annotation { "Feature Type Name" : "Feature", "Feature Type Description" : "" }
export const myFeature = defineFeature(function(context is Context, id is Id, definition is map)
    precondition{}
    {
        {
            var Q0;
            Q0=qCreatedBy(makeId("Top.planeOp"),FACE);
            var sketch = newSketch(context, id + "F0", { "sketchPlane" : qUnion([Q0])});
            skLineSegment(sketch, "E0", {"start": v(-28.2, 6.74) * mm, "end": v(-29.58, 6.6) * mm});
            skLineSegment(sketch, "E1", {"start": v(-29.58, 6.6) * mm, "end": v(-30.85, 6.2) * mm});
            skLineSegment(sketch, "E2", {"start": v(-30.85, 6.2) * mm, "end": v(-32, 5.59) * mm});
            skLineSegment(sketch, "E3", {"start": v(-32, 5.59) * mm, "end": v(-33.01, 4.76) * mm});
            skLineSegment(sketch, "E4", {"start": v(-33.01, 4.76) * mm, "end": v(-33.84, 3.77) * mm});
            skLineSegment(sketch, "E5", {"start": v(-33.84, 3.77) * mm, "end": v(-34.47, 2.62) * mm});
            skLineSegment(sketch, "E6", {"start": v(-34.47, 2.62) * mm, "end": v(-34.86, 1.36) * mm});
            skLineSegment(sketch, "E7", {"start": v(-34.86, 1.36) * mm, "end": v(-35, 0) * mm});
            skLineSegment(sketch, "E8", {"start": v(-35, 0) * mm, "end": v(-34.86, -1.36) * mm});
            skLineSegment(sketch, "E9", {"start": v(-34.86, -1.36) * mm, "end": v(-34.47, -2.62) * mm});
            skLineSegment(sketch, "E10", {"start": v(-34.47, -2.62) * mm, "end": v(-33.84, -3.77) * mm});
            skLineSegment(sketch, "E11", {"start": v(-33.84, -3.77) * mm, "end": v(-33.01, -4.76) * mm});
            skLineSegment(sketch, "E12", {"start": v(-33.01, -4.76) * mm, "end": v(-32, -5.59) * mm});
            skLineSegment(sketch, "E13", {"start": v(-32, -5.59) * mm, "end": v(-30.85, -6.2) * mm});
            skLineSegment(sketch, "E14", {"start": v(-30.85, -6.2) * mm, "end": v(-29.58, -6.6) * mm});
            skLineSegment(sketch, "E15", {"start": v(-29.58, -6.6) * mm, "end": v(-28.2, -6.74) * mm});
            skLineSegment(sketch, "E16", {"start": v(-28.2, -6.74) * mm, "end": v(-26.84, -6.6) * mm});
            skLineSegment(sketch, "E17", {"start": v(-26.84, -6.6) * mm, "end": v(-25.56, -6.2) * mm});
            skLineSegment(sketch, "E18", {"start": v(-25.56, -6.2) * mm, "end": v(-24.41, -5.59) * mm});
            skLineSegment(sketch, "E19", {"start": v(-24.41, -5.59) * mm, "end": v(-23.4, -4.76) * mm});
            skLineSegment(sketch, "E20", {"start": v(-23.4, -4.76) * mm, "end": v(-22.58, -3.77) * mm});
            skLineSegment(sketch, "E21", {"start": v(-22.58, -3.77) * mm, "end": v(-21.95, -2.62) * mm});
            skLineSegment(sketch, "E22", {"start": v(-21.95, -2.62) * mm, "end": v(-21.55, -1.36) * mm});
            skLineSegment(sketch, "E23", {"start": v(-21.55, -1.36) * mm, "end": v(-21.42, 0) * mm});
            skLineSegment(sketch, "E24", {"start": v(-21.42, 0) * mm, "end": v(-21.55, 1.36) * mm});
            skLineSegment(sketch, "E25", {"start": v(-21.55, 1.36) * mm, "end": v(-21.95, 2.62) * mm});
            skLineSegment(sketch, "E26", {"start": v(-21.95, 2.62) * mm, "end": v(-22.58, 3.77) * mm});
            skLineSegment(sketch, "E27", {"start": v(-22.58, 3.77) * mm, "end": v(-23.4, 4.76) * mm});
            skLineSegment(sketch, "E28", {"start": v(-23.4, 4.76) * mm, "end": v(-24.41, 5.59) * mm});
            skLineSegment(sketch, "E29", {"start": v(-24.41, 5.59) * mm, "end": v(-25.56, 6.2) * mm});
            skLineSegment(sketch, "E30", {"start": v(-25.56, 6.2) * mm, "end": v(-26.84, 6.6) * mm});
            skLineSegment(sketch, "E31", {"start": v(-26.84, 6.6) * mm, "end": v(-28.2, 6.74) * mm});
            skLineSegment(sketch, "E32", {"start": v(-28.2, -6.34) * mm, "end": v(-29.5, -6.21) * mm});
            skLineSegment(sketch, "E33", {"start": v(-29.5, -6.21) * mm, "end": v(-30.7, -5.84) * mm});
            skLineSegment(sketch, "E34", {"start": v(-30.7, -5.84) * mm, "end": v(-31.78, -5.26) * mm});
            skLineSegment(sketch, "E35", {"start": v(-31.78, -5.26) * mm, "end": v(-32.73, -4.48) * mm});
            skLineSegment(sketch, "E36", {"start": v(-32.73, -4.48) * mm, "end": v(-33.5, -3.54) * mm});
            skLineSegment(sketch, "E37", {"start": v(-33.5, -3.54) * mm, "end": v(-34.1, -2.47) * mm});
            skLineSegment(sketch, "E38", {"start": v(-34.1, -2.47) * mm, "end": v(-34.47, -1.28) * mm});
            skLineSegment(sketch, "E39", {"start": v(-34.47, -1.28) * mm, "end": v(-34.6, 0) * mm});
            skLineSegment(sketch, "E40", {"start": v(-34.6, 0) * mm, "end": v(-34.47, 1.28) * mm});
            skLineSegment(sketch, "E41", {"start": v(-34.47, 1.28) * mm, "end": v(-34.1, 2.47) * mm});
            skLineSegment(sketch, "E42", {"start": v(-34.1, 2.47) * mm, "end": v(-33.5, 3.54) * mm});
            skLineSegment(sketch, "E43", {"start": v(-33.5, 3.54) * mm, "end": v(-32.73, 4.48) * mm});
            skLineSegment(sketch, "E44", {"start": v(-32.73, 4.48) * mm, "end": v(-31.78, 5.25) * mm});
            skLineSegment(sketch, "E45", {"start": v(-31.78, 5.25) * mm, "end": v(-30.7, 5.84) * mm});
            skLineSegment(sketch, "E46", {"start": v(-30.7, 5.84) * mm, "end": v(-29.5, 6.2) * mm});
            skLineSegment(sketch, "E47", {"start": v(-29.5, 6.2) * mm, "end": v(-28.2, 6.34) * mm});
            skLineSegment(sketch, "E48", {"start": v(-28.2, 6.34) * mm, "end": v(-26.92, 6.2) * mm});
            skLineSegment(sketch, "E49", {"start": v(-26.92, 6.2) * mm, "end": v(-25.72, 5.84) * mm});
            skLineSegment(sketch, "E50", {"start": v(-25.72, 5.84) * mm, "end": v(-24.64, 5.25) * mm});
            skLineSegment(sketch, "E51", {"start": v(-24.64, 5.25) * mm, "end": v(-23.69, 4.48) * mm});
            skLineSegment(sketch, "E52", {"start": v(-23.69, 4.48) * mm, "end": v(-22.9, 3.54) * mm});
            skLineSegment(sketch, "E53", {"start": v(-22.9, 3.54) * mm, "end": v(-22.32, 2.47) * mm});
            skLineSegment(sketch, "E54", {"start": v(-22.32, 2.47) * mm, "end": v(-21.95, 1.28) * mm});
            skLineSegment(sketch, "E55", {"start": v(-21.95, 1.28) * mm, "end": v(-21.82, 0) * mm});
            skLineSegment(sketch, "E56", {"start": v(-21.82, 0) * mm, "end": v(-21.95, -1.28) * mm});
            skLineSegment(sketch, "E57", {"start": v(-21.95, -1.28) * mm, "end": v(-22.32, -2.47) * mm});
            skLineSegment(sketch, "E58", {"start": v(-22.32, -2.47) * mm, "end": v(-22.9, -3.54) * mm});
            skLineSegment(sketch, "E59", {"start": v(-22.9, -3.54) * mm, "end": v(-23.69, -4.48) * mm});
            skLineSegment(sketch, "E60", {"start": v(-23.69, -4.48) * mm, "end": v(-24.64, -5.26) * mm});
            skLineSegment(sketch, "E61", {"start": v(-24.64, -5.26) * mm, "end": v(-25.72, -5.84) * mm});
            skLineSegment(sketch, "E62", {"start": v(-25.72, -5.84) * mm, "end": v(-26.92, -6.21) * mm});
            skLineSegment(sketch, "E63", {"start": v(-26.92, -6.21) * mm, "end": v(-28.2, -6.34) * mm});
            skLineSegment(sketch, "E64", {"start": v(-28.76, -0.16) * mm, "end": v(-28.83, -0.32) * mm});
            skLineSegment(sketch, "E65", {"start": v(-28.83, -0.32) * mm, "end": v(-28.9, -0.48) * mm});
            skLineSegment(sketch, "E66", {"start": v(-28.9, -0.48) * mm, "end": v(-30.52, 0.36) * mm});
            skLineSegment(sketch, "E67", {"start": v(-30.52, 0.36) * mm, "end": v(-32.13, 1.2) * mm});
            skLineSegment(sketch, "E68", {"start": v(-32.13, 1.2) * mm, "end": v(-30.96, -0.3) * mm});
            skLineSegment(sketch, "E69", {"start": v(-30.96, -0.3) * mm, "end": v(-29.8, -1.79) * mm});
            skLineSegment(sketch, "E70", {"start": v(-29.8, -1.79) * mm, "end": v(-30.4, -1.85) * mm});
            skLineSegment(sketch, "E71", {"start": v(-30.4, -1.85) * mm, "end": v(-30.98, -1.92) * mm});
            skLineSegment(sketch, "E72", {"start": v(-30.98, -1.92) * mm, "end": v(-30.66, -2.5) * mm});
            skLineSegment(sketch, "E73", {"start": v(-30.66, -2.5) * mm, "end": v(-30.32, -3.1) * mm});
            skLineSegment(sketch, "E74", {"start": v(-30.32, -3.1) * mm, "end": v(-32, -3.65) * mm});
            skLineSegment(sketch, "E75", {"start": v(-32, -3.65) * mm, "end": v(-32.6, -3.84) * mm});
            skLineSegment(sketch, "E76", {"start": v(-32.6, -3.84) * mm, "end": v(-32.92, -3.45) * mm});
            skLineSegment(sketch, "E77", {"start": v(-32.92, -3.45) * mm, "end": v(-33.2, -3.02) * mm});
            skLineSegment(sketch, "E78", {"start": v(-33.2, -3.02) * mm, "end": v(-33.46, -2.57) * mm});
            skLineSegment(sketch, "E79", {"start": v(-33.46, -2.57) * mm, "end": v(-33.67, -2.1) * mm});
            skLineSegment(sketch, "E80", {"start": v(-33.67, -2.1) * mm, "end": v(-33.84, -1.6) * mm});
            skLineSegment(sketch, "E81", {"start": v(-33.84, -1.6) * mm, "end": v(-33.96, -1.08) * mm});
            skLineSegment(sketch, "E82", {"start": v(-33.96, -1.08) * mm, "end": v(-34.04, -0.55) * mm});
            skLineSegment(sketch, "E83", {"start": v(-34.04, -0.55) * mm, "end": v(-34.06, 0) * mm});
            skLineSegment(sketch, "E84", {"start": v(-34.06, 0) * mm, "end": v(-34.02, 0.7) * mm});
            skLineSegment(sketch, "E85", {"start": v(-34.02, 0.7) * mm, "end": v(-33.9, 1.39) * mm});
            skLineSegment(sketch, "E86", {"start": v(-33.9, 1.39) * mm, "end": v(-33.69, 2.04) * mm});
            skLineSegment(sketch, "E87", {"start": v(-33.69, 2.04) * mm, "end": v(-33.41, 2.66) * mm});
            skLineSegment(sketch, "E88", {"start": v(-33.41, 2.66) * mm, "end": v(-33.07, 3.24) * mm});
            skLineSegment(sketch, "E89", {"start": v(-33.07, 3.24) * mm, "end": v(-32.66, 3.77) * mm});
            skLineSegment(sketch, "E90", {"start": v(-32.66, 3.77) * mm, "end": v(-32.2, 4.25) * mm});
            skLineSegment(sketch, "E91", {"start": v(-32.2, 4.25) * mm, "end": v(-31.68, 4.67) * mm});
            skLineSegment(sketch, "E92", {"start": v(-31.68, 4.67) * mm, "end": v(-30.23, 2.25) * mm});
            skLineSegment(sketch, "E93", {"start": v(-30.23, 2.25) * mm, "end": v(-28.76, -0.16) * mm});
            skLineSegment(sketch, "E94", {"start": v(-22.36, 0) * mm, "end": v(-22.47, -1.17) * mm});
            skLineSegment(sketch, "E95", {"start": v(-22.47, -1.17) * mm, "end": v(-22.82, -2.26) * mm});
            skLineSegment(sketch, "E96", {"start": v(-22.82, -2.26) * mm, "end": v(-23.36, -3.25) * mm});
            skLineSegment(sketch, "E97", {"start": v(-23.36, -3.25) * mm, "end": v(-24.07, -4.1) * mm});
            skLineSegment(sketch, "E98", {"start": v(-24.07, -4.1) * mm, "end": v(-24.94, -4.81) * mm});
            skLineSegment(sketch, "E99", {"start": v(-24.94, -4.81) * mm, "end": v(-25.93, -5.35) * mm});
            skLineSegment(sketch, "E100", {"start": v(-25.93, -5.35) * mm, "end": v(-27.03, -5.69) * mm});
            skLineSegment(sketch, "E101", {"start": v(-27.03, -5.69) * mm, "end": v(-28.21, -5.8) * mm});
            skLineSegment(sketch, "E102", {"start": v(-28.21, -5.8) * mm, "end": v(-28.75, -5.78) * mm});
            skLineSegment(sketch, "E103", {"start": v(-28.75, -5.78) * mm, "end": v(-29.28, -5.71) * mm});
            skLineSegment(sketch, "E104", {"start": v(-29.28, -5.71) * mm, "end": v(-29.79, -5.6) * mm});
            skLineSegment(sketch, "E105", {"start": v(-29.79, -5.6) * mm, "end": v(-30.28, -5.43) * mm});
            skLineSegment(sketch, "E106", {"start": v(-30.28, -5.43) * mm, "end": v(-30.75, -5.23) * mm});
            skLineSegment(sketch, "E107", {"start": v(-30.75, -5.23) * mm, "end": v(-31.2, -4.99) * mm});
            skLineSegment(sketch, "E108", {"start": v(-31.2, -4.99) * mm, "end": v(-31.63, -4.71) * mm});
            skLineSegment(sketch, "E109", {"start": v(-31.63, -4.71) * mm, "end": v(-32.03, -4.4) * mm});
            skLineSegment(sketch, "E110", {"start": v(-32.03, -4.4) * mm, "end": v(-31.85, -4.42) * mm});
            skLineSegment(sketch, "E111", {"start": v(-31.85, -4.42) * mm, "end": v(-30.03, -4.64) * mm});
            skLineSegment(sketch, "E112", {"start": v(-30.03, -4.64) * mm, "end": v(-23.6, -1.32) * mm});
            skLineSegment(sketch, "E113", {"start": v(-23.6, -1.32) * mm, "end": v(-22.53, 0.74) * mm});
            skLineSegment(sketch, "E114", {"start": v(-22.53, 0.74) * mm, "end": v(-22.43, 0.93) * mm});
            skLineSegment(sketch, "E115", {"start": v(-22.43, 0.93) * mm, "end": v(-22.36, 0) * mm});
            skLineSegment(sketch, "E116", {"start": v(-22.58, 1.6) * mm, "end": v(-23.88, 0.4) * mm});
            skLineSegment(sketch, "E117", {"start": v(-23.88, 0.4) * mm, "end": v(-24.35, 0) * mm});
            skLineSegment(sketch, "E118", {"start": v(-24.35, 0) * mm, "end": v(-24.64, -0.26) * mm});
            skLineSegment(sketch, "E119", {"start": v(-24.64, -0.26) * mm, "end": v(-24.95, 0.87) * mm});
            skLineSegment(sketch, "E120", {"start": v(-24.95, 0.87) * mm, "end": v(-25.64, 0.4) * mm});
            skLineSegment(sketch, "E121", {"start": v(-25.64, 0.4) * mm, "end": v(-26.1, 0.1) * mm});
            skLineSegment(sketch, "E122", {"start": v(-26.1, 0.1) * mm, "end": v(-27.26, 3.8) * mm});
            skLineSegment(sketch, "E123", {"start": v(-27.26, 3.8) * mm, "end": v(-27.59, 0.22) * mm});
            skLineSegment(sketch, "E124", {"start": v(-27.59, 0.22) * mm, "end": v(-27.98, 0.4) * mm});
            skLineSegment(sketch, "E125", {"start": v(-27.98, 0.4) * mm, "end": v(-29.46, 2.6) * mm});
            skLineSegment(sketch, "E126", {"start": v(-29.46, 2.6) * mm, "end": v(-30.97, 5.12) * mm});
            skLineSegment(sketch, "E127", {"start": v(-30.97, 5.12) * mm, "end": v(-30.66, 5.27) * mm});
            skLineSegment(sketch, "E128", {"start": v(-30.66, 5.27) * mm, "end": v(-30.34, 5.41) * mm});
            skLineSegment(sketch, "E129", {"start": v(-30.34, 5.41) * mm, "end": v(-30, 5.53) * mm});
            skLineSegment(sketch, "E130", {"start": v(-30, 5.53) * mm, "end": v(-29.66, 5.63) * mm});
            skLineSegment(sketch, "E131", {"start": v(-29.66, 5.63) * mm, "end": v(-29.3, 5.7) * mm});
            skLineSegment(sketch, "E132", {"start": v(-29.3, 5.7) * mm, "end": v(-28.95, 5.76) * mm});
            skLineSegment(sketch, "E133", {"start": v(-28.95, 5.76) * mm, "end": v(-28.58, 5.8) * mm});
            skLineSegment(sketch, "E134", {"start": v(-28.58, 5.8) * mm, "end": v(-28.21, 5.8) * mm});
            skLineSegment(sketch, "E135", {"start": v(-28.21, 5.8) * mm, "end": v(-27.23, 5.72) * mm});
            skLineSegment(sketch, "E136", {"start": v(-27.23, 5.72) * mm, "end": v(-26.3, 5.49) * mm});
            skLineSegment(sketch, "E137", {"start": v(-26.3, 5.49) * mm, "end": v(-25.44, 5.11) * mm});
            skLineSegment(sketch, "E138", {"start": v(-25.44, 5.11) * mm, "end": v(-24.65, 4.6) * mm});
            skLineSegment(sketch, "E139", {"start": v(-24.65, 4.6) * mm, "end": v(-23.96, 4) * mm});
            skLineSegment(sketch, "E140", {"start": v(-23.96, 4) * mm, "end": v(-23.38, 3.28) * mm});
            skLineSegment(sketch, "E141", {"start": v(-23.38, 3.28) * mm, "end": v(-22.91, 2.47) * mm});
            skLineSegment(sketch, "E142", {"start": v(-22.91, 2.47) * mm, "end": v(-22.58, 1.6) * mm});
            skLineSegment(sketch, "E143", {"start": v(-18.1, 2.47) * mm, "end": v(-15.89, 2.47) * mm});
            skLineSegment(sketch, "E144", {"start": v(-15.89, 2.47) * mm, "end": v(-15.89, 1.41) * mm});
            skLineSegment(sketch, "E145", {"start": v(-15.89, 1.41) * mm, "end": v(-18, 1.41) * mm});
            skLineSegment(sketch, "E146", {"start": v(-18, 1.41) * mm, "end": v(-18.15, 1.4) * mm});
            skLineSegment(sketch, "E147", {"start": v(-18.15, 1.4) * mm, "end": v(-18.27, 1.38) * mm});
            skLineSegment(sketch, "E148", {"start": v(-18.27, 1.38) * mm, "end": v(-18.37, 1.33) * mm});
            skLineSegment(sketch, "E149", {"start": v(-18.37, 1.33) * mm, "end": v(-18.46, 1.26) * mm});
            skLineSegment(sketch, "E150", {"start": v(-18.46, 1.26) * mm, "end": v(-18.52, 1.17) * mm});
            skLineSegment(sketch, "E151", {"start": v(-18.52, 1.17) * mm, "end": v(-18.57, 1.07) * mm});
            skLineSegment(sketch, "E152", {"start": v(-18.57, 1.07) * mm, "end": v(-18.6, 0.95) * mm});
            skLineSegment(sketch, "E153", {"start": v(-18.6, 0.95) * mm, "end": v(-18.6, 0.8) * mm});
            skLineSegment(sketch, "E154", {"start": v(-18.6, 0.8) * mm, "end": v(-18.6, -0.9) * mm});
            skLineSegment(sketch, "E155", {"start": v(-18.6, -0.9) * mm, "end": v(-18.6, -1.05) * mm});
            skLineSegment(sketch, "E156", {"start": v(-18.6, -1.05) * mm, "end": v(-18.57, -1.17) * mm});
            skLineSegment(sketch, "E157", {"start": v(-18.57, -1.17) * mm, "end": v(-18.52, -1.27) * mm});
            skLineSegment(sketch, "E158", {"start": v(-18.52, -1.27) * mm, "end": v(-18.46, -1.36) * mm});
            skLineSegment(sketch, "E159", {"start": v(-18.46, -1.36) * mm, "end": v(-18.37, -1.42) * mm});
            skLineSegment(sketch, "E160", {"start": v(-18.37, -1.42) * mm, "end": v(-18.27, -1.47) * mm});
            skLineSegment(sketch, "E161", {"start": v(-18.27, -1.47) * mm, "end": v(-18.15, -1.5) * mm});
            skLineSegment(sketch, "E162", {"start": v(-18.15, -1.5) * mm, "end": v(-18, -1.5) * mm});
            skLineSegment(sketch, "E163", {"start": v(-18, -1.5) * mm, "end": v(-15.89, -1.5) * mm});
            skLineSegment(sketch, "E164", {"start": v(-15.89, -1.5) * mm, "end": v(-15.89, -2.57) * mm});
            skLineSegment(sketch, "E165", {"start": v(-15.89, -2.57) * mm, "end": v(-18.1, -2.57) * mm});
            skLineSegment(sketch, "E166", {"start": v(-18.1, -2.57) * mm, "end": v(-18.29, -2.56) * mm});
            skLineSegment(sketch, "E167", {"start": v(-18.29, -2.56) * mm, "end": v(-18.46, -2.54) * mm});
            skLineSegment(sketch, "E168", {"start": v(-18.46, -2.54) * mm, "end": v(-18.62, -2.5) * mm});
            skLineSegment(sketch, "E169", {"start": v(-18.62, -2.5) * mm, "end": v(-18.77, -2.46) * mm});
            skLineSegment(sketch, "E170", {"start": v(-18.77, -2.46) * mm, "end": v(-18.9, -2.4) * mm});
            skLineSegment(sketch, "E171", {"start": v(-18.9, -2.4) * mm, "end": v(-19.04, -2.33) * mm});
            skLineSegment(sketch, "E172", {"start": v(-19.04, -2.33) * mm, "end": v(-19.15, -2.25) * mm});
            skLineSegment(sketch, "E173", {"start": v(-19.15, -2.25) * mm, "end": v(-19.26, -2.15) * mm});
            skLineSegment(sketch, "E174", {"start": v(-19.26, -2.15) * mm, "end": v(-19.36, -2.04) * mm});
            skLineSegment(sketch, "E175", {"start": v(-19.36, -2.04) * mm, "end": v(-19.45, -1.92) * mm});
            skLineSegment(sketch, "E176", {"start": v(-19.45, -1.92) * mm, "end": v(-19.52, -1.79) * mm});
            skLineSegment(sketch, "E177", {"start": v(-19.52, -1.79) * mm, "end": v(-19.58, -1.65) * mm});
            skLineSegment(sketch, "E178", {"start": v(-19.58, -1.65) * mm, "end": v(-19.62, -1.5) * mm});
            skLineSegment(sketch, "E179", {"start": v(-19.62, -1.5) * mm, "end": v(-19.66, -1.34) * mm});
            skLineSegment(sketch, "E180", {"start": v(-19.66, -1.34) * mm, "end": v(-19.68, -1.17) * mm});
            skLineSegment(sketch, "E181", {"start": v(-19.68, -1.17) * mm, "end": v(-19.68, -0.99) * mm});
            skLineSegment(sketch, "E182", {"start": v(-19.68, -0.99) * mm, "end": v(-19.68, 0.9) * mm});
            skLineSegment(sketch, "E183", {"start": v(-19.68, 0.9) * mm, "end": v(-19.68, 1.07) * mm});
            skLineSegment(sketch, "E184", {"start": v(-19.68, 1.07) * mm, "end": v(-19.66, 1.24) * mm});
            skLineSegment(sketch, "E185", {"start": v(-19.66, 1.24) * mm, "end": v(-19.62, 1.4) * mm});
            skLineSegment(sketch, "E186", {"start": v(-19.62, 1.4) * mm, "end": v(-19.58, 1.55) * mm});
            skLineSegment(sketch, "E187", {"start": v(-19.58, 1.55) * mm, "end": v(-19.52, 1.7) * mm});
            skLineSegment(sketch, "E188", {"start": v(-19.52, 1.7) * mm, "end": v(-19.45, 1.82) * mm});
            skLineSegment(sketch, "E189", {"start": v(-19.45, 1.82) * mm, "end": v(-19.36, 1.94) * mm});
            skLineSegment(sketch, "E190", {"start": v(-19.36, 1.94) * mm, "end": v(-19.26, 2.05) * mm});
            skLineSegment(sketch, "E191", {"start": v(-19.26, 2.05) * mm, "end": v(-19.15, 2.15) * mm});
            skLineSegment(sketch, "E192", {"start": v(-19.15, 2.15) * mm, "end": v(-19.04, 2.23) * mm});
            skLineSegment(sketch, "E193", {"start": v(-19.04, 2.23) * mm, "end": v(-18.9, 2.3) * mm});
            skLineSegment(sketch, "E194", {"start": v(-18.9, 2.3) * mm, "end": v(-18.77, 2.36) * mm});
            skLineSegment(sketch, "E195", {"start": v(-18.77, 2.36) * mm, "end": v(-18.62, 2.4) * mm});
            skLineSegment(sketch, "E196", {"start": v(-18.62, 2.4) * mm, "end": v(-18.46, 2.44) * mm});
            skLineSegment(sketch, "E197", {"start": v(-18.46, 2.44) * mm, "end": v(-18.29, 2.46) * mm});
            skLineSegment(sketch, "E198", {"start": v(-18.29, 2.46) * mm, "end": v(-18.1, 2.47) * mm});
            skLineSegment(sketch, "E199", {"start": v(-15.34, 2.47) * mm, "end": v(-12.56, 2.47) * mm});
            skLineSegment(sketch, "E200", {"start": v(-12.56, 2.47) * mm, "end": v(-12.2, 2.45) * mm});
            skLineSegment(sketch, "E201", {"start": v(-12.2, 2.45) * mm, "end": v(-11.88, 2.4) * mm});
            skLineSegment(sketch, "E202", {"start": v(-11.88, 2.4) * mm, "end": v(-11.74, 2.36) * mm});
            skLineSegment(sketch, "E203", {"start": v(-11.74, 2.36) * mm, "end": v(-11.61, 2.31) * mm});
            skLineSegment(sketch, "E204", {"start": v(-11.61, 2.31) * mm, "end": v(-11.5, 2.26) * mm});
            skLineSegment(sketch, "E205", {"start": v(-11.5, 2.26) * mm, "end": v(-11.4, 2.2) * mm});
            skLineSegment(sketch, "E206", {"start": v(-11.4, 2.2) * mm, "end": v(-11.31, 2.12) * mm});
            skLineSegment(sketch, "E207", {"start": v(-11.31, 2.12) * mm, "end": v(-11.23, 2.04) * mm});
            skLineSegment(sketch, "E208", {"start": v(-11.23, 2.04) * mm, "end": v(-11.17, 1.95) * mm});
            skLineSegment(sketch, "E209", {"start": v(-11.17, 1.95) * mm, "end": v(-11.12, 1.85) * mm});
            skLineSegment(sketch, "E210", {"start": v(-11.12, 1.85) * mm, "end": v(-11.08, 1.74) * mm});
            skLineSegment(sketch, "E211", {"start": v(-11.08, 1.74) * mm, "end": v(-11.05, 1.62) * mm});
            skLineSegment(sketch, "E212", {"start": v(-11.05, 1.62) * mm, "end": v(-11.03, 1.5) * mm});
            skLineSegment(sketch, "E213", {"start": v(-11.03, 1.5) * mm, "end": v(-11.02, 1.36) * mm});
            skLineSegment(sketch, "E214", {"start": v(-11.02, 1.36) * mm, "end": v(-11.02, 0.96) * mm});
            skLineSegment(sketch, "E215", {"start": v(-11.02, 0.96) * mm, "end": v(-11.03, 0.75) * mm});
            skLineSegment(sketch, "E216", {"start": v(-11.03, 0.75) * mm, "end": v(-11.06, 0.56) * mm});
            skLineSegment(sketch, "E217", {"start": v(-11.06, 0.56) * mm, "end": v(-11.11, 0.4) * mm});
            skLineSegment(sketch, "E218", {"start": v(-11.11, 0.4) * mm, "end": v(-11.19, 0.26) * mm});
            skLineSegment(sketch, "E219", {"start": v(-11.19, 0.26) * mm, "end": v(-11.28, 0.14) * mm});
            skLineSegment(sketch, "E220", {"start": v(-11.28, 0.14) * mm, "end": v(-11.4, 0.04) * mm});
            skLineSegment(sketch, "E221", {"start": v(-11.4, 0.04) * mm, "end": v(-11.53, -0.04) * mm});
            skLineSegment(sketch, "E222", {"start": v(-11.53, -0.04) * mm, "end": v(-11.68, -0.1) * mm});
            skLineSegment(sketch, "E223", {"start": v(-11.68, -0.1) * mm, "end": v(-11.58, -0.15) * mm});
            skLineSegment(sketch, "E224", {"start": v(-11.58, -0.15) * mm, "end": v(-11.5, -0.21) * mm});
            skLineSegment(sketch, "E225", {"start": v(-11.5, -0.21) * mm, "end": v(-11.41, -0.29) * mm});
            skLineSegment(sketch, "E226", {"start": v(-11.41, -0.29) * mm, "end": v(-11.34, -0.38) * mm});
            skLineSegment(sketch, "E227", {"start": v(-11.34, -0.38) * mm, "end": v(-11.14, -0.87) * mm});
            skLineSegment(sketch, "E228", {"start": v(-11.14, -0.87) * mm, "end": v(-10.78, -2.57) * mm});
            skLineSegment(sketch, "E229", {"start": v(-10.78, -2.57) * mm, "end": v(-11.9, -2.57) * mm});
            skLineSegment(sketch, "E230", {"start": v(-11.9, -2.57) * mm, "end": v(-12.16, -1.2) * mm});
            skLineSegment(sketch, "E231", {"start": v(-12.16, -1.2) * mm, "end": v(-12.18, -1.07) * mm});
            skLineSegment(sketch, "E232", {"start": v(-12.18, -1.07) * mm, "end": v(-12.23, -0.95) * mm});
            skLineSegment(sketch, "E233", {"start": v(-12.23, -0.95) * mm, "end": v(-12.28, -0.85) * mm});
            skLineSegment(sketch, "E234", {"start": v(-12.28, -0.85) * mm, "end": v(-12.35, -0.76) * mm});
            skLineSegment(sketch, "E235", {"start": v(-12.35, -0.76) * mm, "end": v(-12.42, -0.68) * mm});
            skLineSegment(sketch, "E236", {"start": v(-12.42, -0.68) * mm, "end": v(-12.5, -0.63) * mm});
            skLineSegment(sketch, "E237", {"start": v(-12.5, -0.63) * mm, "end": v(-12.59, -0.6) * mm});
            skLineSegment(sketch, "E238", {"start": v(-12.59, -0.6) * mm, "end": v(-12.68, -0.59) * mm});
            skLineSegment(sketch, "E239", {"start": v(-12.68, -0.59) * mm, "end": v(-13.76, -0.59) * mm});
            skLineSegment(sketch, "E240", {"start": v(-13.76, -0.59) * mm, "end": v(-13.76, 0.42) * mm});
            skLineSegment(sketch, "E241", {"start": v(-13.76, 0.42) * mm, "end": v(-12.6, 0.42) * mm});
            skLineSegment(sketch, "E242", {"start": v(-12.6, 0.42) * mm, "end": v(-12.5, 0.43) * mm});
            skLineSegment(sketch, "E243", {"start": v(-12.5, 0.43) * mm, "end": v(-12.39, 0.44) * mm});
            skLineSegment(sketch, "E244", {"start": v(-12.39, 0.44) * mm, "end": v(-12.3, 0.47) * mm});
            skLineSegment(sketch, "E245", {"start": v(-12.3, 0.47) * mm, "end": v(-12.23, 0.51) * mm});
            skLineSegment(sketch, "E246", {"start": v(-12.23, 0.51) * mm, "end": v(-12.17, 0.57) * mm});
            skLineSegment(sketch, "E247", {"start": v(-12.17, 0.57) * mm, "end": v(-12.13, 0.63) * mm});
            skLineSegment(sketch, "E248", {"start": v(-12.13, 0.63) * mm, "end": v(-12.1, 0.7) * mm});
            skLineSegment(sketch, "E249", {"start": v(-12.1, 0.7) * mm, "end": v(-12.1, 0.78) * mm});
            skLineSegment(sketch, "E250", {"start": v(-12.1, 0.78) * mm, "end": v(-12.1, 1.05) * mm});
            skLineSegment(sketch, "E251", {"start": v(-12.1, 1.05) * mm, "end": v(-12.1, 1.13) * mm});
            skLineSegment(sketch, "E252", {"start": v(-12.1, 1.13) * mm, "end": v(-12.13, 1.2) * mm});
            skLineSegment(sketch, "E253", {"start": v(-12.13, 1.2) * mm, "end": v(-12.17, 1.27) * mm});
            skLineSegment(sketch, "E254", {"start": v(-12.17, 1.27) * mm, "end": v(-12.23, 1.32) * mm});
            skLineSegment(sketch, "E255", {"start": v(-12.23, 1.32) * mm, "end": v(-12.3, 1.36) * mm});
            skLineSegment(sketch, "E256", {"start": v(-12.3, 1.36) * mm, "end": v(-12.39, 1.4) * mm});
            skLineSegment(sketch, "E257", {"start": v(-12.39, 1.4) * mm, "end": v(-12.5, 1.4) * mm});
            skLineSegment(sketch, "E258", {"start": v(-12.5, 1.4) * mm, "end": v(-12.6, 1.41) * mm});
            skLineSegment(sketch, "E259", {"start": v(-12.6, 1.41) * mm, "end": v(-14.26, 1.41) * mm});
            skLineSegment(sketch, "E260", {"start": v(-14.26, 1.41) * mm, "end": v(-14.26, -2.57) * mm});
            skLineSegment(sketch, "E261", {"start": v(-14.26, -2.57) * mm, "end": v(-15.34, -2.57) * mm});
            skLineSegment(sketch, "E262", {"start": v(-15.34, -2.57) * mm, "end": v(-15.34, 2.47) * mm});
            skLineSegment(sketch, "E263", {"start": v(-8.8, 2.47) * mm, "end": v(-6.3, 2.47) * mm});
            skLineSegment(sketch, "E264", {"start": v(-6.3, 2.47) * mm, "end": v(-6.3, 1.41) * mm});
            skLineSegment(sketch, "E265", {"start": v(-6.3, 1.41) * mm, "end": v(-8.7, 1.41) * mm});
            skLineSegment(sketch, "E266", {"start": v(-8.7, 1.41) * mm, "end": v(-8.86, 1.4) * mm});
            skLineSegment(sketch, "E267", {"start": v(-8.86, 1.4) * mm, "end": v(-8.99, 1.38) * mm});
            skLineSegment(sketch, "E268", {"start": v(-8.99, 1.38) * mm, "end": v(-9.09, 1.34) * mm});
            skLineSegment(sketch, "E269", {"start": v(-9.09, 1.34) * mm, "end": v(-9.16, 1.29) * mm});
            skLineSegment(sketch, "E270", {"start": v(-9.16, 1.29) * mm, "end": v(-9.22, 1.21) * mm});
            skLineSegment(sketch, "E271", {"start": v(-9.22, 1.21) * mm, "end": v(-9.26, 1.11) * mm});
            skLineSegment(sketch, "E272", {"start": v(-9.26, 1.11) * mm, "end": v(-9.28, 0.98) * mm});
            skLineSegment(sketch, "E273", {"start": v(-9.28, 0.98) * mm, "end": v(-9.29, 0.83) * mm});
            skLineSegment(sketch, "E274", {"start": v(-9.29, 0.83) * mm, "end": v(-9.29, 0.5) * mm});
            skLineSegment(sketch, "E275", {"start": v(-9.29, 0.5) * mm, "end": v(-6.3, 0.5) * mm});
            skLineSegment(sketch, "E276", {"start": v(-6.3, 0.5) * mm, "end": v(-6.3, -0.55) * mm});
            skLineSegment(sketch, "E277", {"start": v(-6.3, -0.55) * mm, "end": v(-9.29, -0.55) * mm});
            skLineSegment(sketch, "E278", {"start": v(-9.29, -0.55) * mm, "end": v(-9.29, -0.93) * mm});
            skLineSegment(sketch, "E279", {"start": v(-9.29, -0.93) * mm, "end": v(-9.28, -1.08) * mm});
            skLineSegment(sketch, "E280", {"start": v(-9.28, -1.08) * mm, "end": v(-9.26, -1.2) * mm});
            skLineSegment(sketch, "E281", {"start": v(-9.26, -1.2) * mm, "end": v(-9.22, -1.3) * mm});
            skLineSegment(sketch, "E282", {"start": v(-9.22, -1.3) * mm, "end": v(-9.16, -1.38) * mm});
            skLineSegment(sketch, "E283", {"start": v(-9.16, -1.38) * mm, "end": v(-9.1, -1.44) * mm});
            skLineSegment(sketch, "E284", {"start": v(-9.1, -1.44) * mm, "end": v(-8.99, -1.48) * mm});
            skLineSegment(sketch, "E285", {"start": v(-8.99, -1.48) * mm, "end": v(-8.86, -1.5) * mm});
            skLineSegment(sketch, "E286", {"start": v(-8.86, -1.5) * mm, "end": v(-8.7, -1.5) * mm});
            skLineSegment(sketch, "E287", {"start": v(-8.7, -1.5) * mm, "end": v(-6.3, -1.5) * mm});
            skLineSegment(sketch, "E288", {"start": v(-6.3, -1.5) * mm, "end": v(-6.3, -2.57) * mm});
            skLineSegment(sketch, "E289", {"start": v(-6.3, -2.57) * mm, "end": v(-8.8, -2.57) * mm});
            skLineSegment(sketch, "E290", {"start": v(-8.8, -2.57) * mm, "end": v(-9, -2.56) * mm});
            skLineSegment(sketch, "E291", {"start": v(-9, -2.56) * mm, "end": v(-9.18, -2.54) * mm});
            skLineSegment(sketch, "E292", {"start": v(-9.18, -2.54) * mm, "end": v(-9.36, -2.52) * mm});
            skLineSegment(sketch, "E293", {"start": v(-9.36, -2.52) * mm, "end": v(-9.52, -2.48) * mm});
            skLineSegment(sketch, "E294", {"start": v(-9.52, -2.48) * mm, "end": v(-9.66, -2.43) * mm});
            skLineSegment(sketch, "E295", {"start": v(-9.66, -2.43) * mm, "end": v(-9.8, -2.36) * mm});
            skLineSegment(sketch, "E296", {"start": v(-9.8, -2.36) * mm, "end": v(-9.9, -2.29) * mm});
            skLineSegment(sketch, "E297", {"start": v(-9.9, -2.29) * mm, "end": v(-10, -2.2) * mm});
            skLineSegment(sketch, "E298", {"start": v(-10, -2.2) * mm, "end": v(-10.09, -2.1) * mm});
            skLineSegment(sketch, "E299", {"start": v(-10.09, -2.1) * mm, "end": v(-10.16, -2) * mm});
            skLineSegment(sketch, "E300", {"start": v(-10.16, -2) * mm, "end": v(-10.22, -1.86) * mm});
            skLineSegment(sketch, "E301", {"start": v(-10.22, -1.86) * mm, "end": v(-10.27, -1.72) * mm});
            skLineSegment(sketch, "E302", {"start": v(-10.27, -1.72) * mm, "end": v(-10.31, -1.56) * mm});
            skLineSegment(sketch, "E303", {"start": v(-10.31, -1.56) * mm, "end": v(-10.34, -1.38) * mm});
            skLineSegment(sketch, "E304", {"start": v(-10.34, -1.38) * mm, "end": v(-10.36, -1.2) * mm});
            skLineSegment(sketch, "E305", {"start": v(-10.36, -1.2) * mm, "end": v(-10.36, -0.99) * mm});
            skLineSegment(sketch, "E306", {"start": v(-10.36, -0.99) * mm, "end": v(-10.36, 0.9) * mm});
            skLineSegment(sketch, "E307", {"start": v(-10.36, 0.9) * mm, "end": v(-10.36, 1.1) * mm});
            skLineSegment(sketch, "E308", {"start": v(-10.36, 1.1) * mm, "end": v(-10.34, 1.29) * mm});
            skLineSegment(sketch, "E309", {"start": v(-10.34, 1.29) * mm, "end": v(-10.31, 1.46) * mm});
            skLineSegment(sketch, "E310", {"start": v(-10.31, 1.46) * mm, "end": v(-10.27, 1.62) * mm});
            skLineSegment(sketch, "E311", {"start": v(-10.27, 1.62) * mm, "end": v(-10.22, 1.77) * mm});
            skLineSegment(sketch, "E312", {"start": v(-10.22, 1.77) * mm, "end": v(-10.16, 1.9) * mm});
            skLineSegment(sketch, "E313", {"start": v(-10.16, 1.9) * mm, "end": v(-10.09, 2) * mm});
            skLineSegment(sketch, "E314", {"start": v(-10.09, 2) * mm, "end": v(-10, 2.1) * mm});
            skLineSegment(sketch, "E315", {"start": v(-10, 2.1) * mm, "end": v(-9.9, 2.2) * mm});
            skLineSegment(sketch, "E316", {"start": v(-9.9, 2.2) * mm, "end": v(-9.8, 2.26) * mm});
            skLineSegment(sketch, "E317", {"start": v(-9.8, 2.26) * mm, "end": v(-9.66, 2.33) * mm});
            skLineSegment(sketch, "E318", {"start": v(-9.66, 2.33) * mm, "end": v(-9.52, 2.38) * mm});
            skLineSegment(sketch, "E319", {"start": v(-9.52, 2.38) * mm, "end": v(-9.36, 2.42) * mm});
            skLineSegment(sketch, "E320", {"start": v(-9.36, 2.42) * mm, "end": v(-9.19, 2.44) * mm});
            skLineSegment(sketch, "E321", {"start": v(-9.19, 2.44) * mm, "end": v(-9, 2.46) * mm});
            skLineSegment(sketch, "E322", {"start": v(-9, 2.46) * mm, "end": v(-8.8, 2.47) * mm});
            skLineSegment(sketch, "E323", {"start": v(-2.49, 1.64) * mm, "end": v(-1.1, -2.57) * mm});
            skLineSegment(sketch, "E324", {"start": v(-1.1, -2.57) * mm, "end": v(-2.23, -2.57) * mm});
            skLineSegment(sketch, "E325", {"start": v(-2.23, -2.57) * mm, "end": v(-3.5, 1.33) * mm});
            skLineSegment(sketch, "E326", {"start": v(-3.5, 1.33) * mm, "end": v(-3.57, 1.47) * mm});
            skLineSegment(sketch, "E327", {"start": v(-3.57, 1.47) * mm, "end": v(-3.7, 1.5) * mm});
            skLineSegment(sketch, "E328", {"start": v(-3.7, 1.5) * mm, "end": v(-3.8, 1.47) * mm});
            skLineSegment(sketch, "E329", {"start": v(-3.8, 1.47) * mm, "end": v(-3.88, 1.33) * mm});
            skLineSegment(sketch, "E330", {"start": v(-3.88, 1.33) * mm, "end": v(-5.14, -2.57) * mm});
            skLineSegment(sketch, "E331", {"start": v(-5.14, -2.57) * mm, "end": v(-6.28, -2.57) * mm});
            skLineSegment(sketch, "E332", {"start": v(-6.28, -2.57) * mm, "end": v(-4.9, 1.64) * mm});
            skLineSegment(sketch, "E333", {"start": v(-4.9, 1.64) * mm, "end": v(-4.8, 1.87) * mm});
            skLineSegment(sketch, "E334", {"start": v(-4.8, 1.87) * mm, "end": v(-4.7, 2.06) * mm});
            skLineSegment(sketch, "E335", {"start": v(-4.7, 2.06) * mm, "end": v(-4.58, 2.22) * mm});
            skLineSegment(sketch, "E336", {"start": v(-4.58, 2.22) * mm, "end": v(-4.45, 2.35) * mm});
            skLineSegment(sketch, "E337", {"start": v(-4.45, 2.35) * mm, "end": v(-4.3, 2.44) * mm});
            skLineSegment(sketch, "E338", {"start": v(-4.3, 2.44) * mm, "end": v(-4.12, 2.51) * mm});
            skLineSegment(sketch, "E339", {"start": v(-4.12, 2.51) * mm, "end": v(-3.92, 2.55) * mm});
            skLineSegment(sketch, "E340", {"start": v(-3.92, 2.55) * mm, "end": v(-3.7, 2.57) * mm});
            skLineSegment(sketch, "E341", {"start": v(-3.7, 2.57) * mm, "end": v(-3.47, 2.55) * mm});
            skLineSegment(sketch, "E342", {"start": v(-3.47, 2.55) * mm, "end": v(-3.26, 2.5) * mm});
            skLineSegment(sketch, "E343", {"start": v(-3.26, 2.5) * mm, "end": v(-3.08, 2.44) * mm});
            skLineSegment(sketch, "E344", {"start": v(-3.08, 2.44) * mm, "end": v(-2.92, 2.33) * mm});
            skLineSegment(sketch, "E345", {"start": v(-2.92, 2.33) * mm, "end": v(-2.78, 2.2) * mm});
            skLineSegment(sketch, "E346", {"start": v(-2.78, 2.2) * mm, "end": v(-2.66, 2.04) * mm});
            skLineSegment(sketch, "E347", {"start": v(-2.66, 2.04) * mm, "end": v(-2.56, 1.86) * mm});
            skLineSegment(sketch, "E348", {"start": v(-2.56, 1.86) * mm, "end": v(-2.49, 1.64) * mm});
            skLineSegment(sketch, "E349", {"start": v(-1.53, 2.47) * mm, "end": v(2.6, 2.47) * mm});
            skLineSegment(sketch, "E350", {"start": v(2.6, 2.47) * mm, "end": v(2.6, 1.41) * mm});
            skLineSegment(sketch, "E351", {"start": v(2.6, 1.41) * mm, "end": v(1.07, 1.41) * mm});
            skLineSegment(sketch, "E352", {"start": v(1.07, 1.41) * mm, "end": v(1.07, -2.57) * mm});
            skLineSegment(sketch, "E353", {"start": v(1.07, -2.57) * mm, "end": v(0, -2.57) * mm});
            skLineSegment(sketch, "E354", {"start": v(0, -2.57) * mm, "end": v(0, 1.41) * mm});
            skLineSegment(sketch, "E355", {"start": v(0, 1.41) * mm, "end": v(-1.53, 1.41) * mm});
            skLineSegment(sketch, "E356", {"start": v(-1.53, 1.41) * mm, "end": v(-1.53, 2.47) * mm});
            skLineSegment(sketch, "E357", {"start": v(4.57, 2.47) * mm, "end": v(7.06, 2.47) * mm});
            skLineSegment(sketch, "E358", {"start": v(7.06, 2.47) * mm, "end": v(7.06, 1.41) * mm});
            skLineSegment(sketch, "E359", {"start": v(7.06, 1.41) * mm, "end": v(4.65, 1.41) * mm});
            skLineSegment(sketch, "E360", {"start": v(4.65, 1.41) * mm, "end": v(4.5, 1.4) * mm});
            skLineSegment(sketch, "E361", {"start": v(4.5, 1.4) * mm, "end": v(4.37, 1.38) * mm});
            skLineSegment(sketch, "E362", {"start": v(4.37, 1.38) * mm, "end": v(4.27, 1.34) * mm});
            skLineSegment(sketch, "E363", {"start": v(4.27, 1.34) * mm, "end": v(4.2, 1.29) * mm});
            skLineSegment(sketch, "E364", {"start": v(4.2, 1.29) * mm, "end": v(4.14, 1.21) * mm});
            skLineSegment(sketch, "E365", {"start": v(4.14, 1.21) * mm, "end": v(4.1, 1.11) * mm});
            skLineSegment(sketch, "E366", {"start": v(4.1, 1.11) * mm, "end": v(4.08, 0.98) * mm});
            skLineSegment(sketch, "E367", {"start": v(4.08, 0.98) * mm, "end": v(4.07, 0.83) * mm});
            skLineSegment(sketch, "E368", {"start": v(4.07, 0.83) * mm, "end": v(4.07, 0.5) * mm});
            skLineSegment(sketch, "E369", {"start": v(4.07, 0.5) * mm, "end": v(7.06, 0.5) * mm});
            skLineSegment(sketch, "E370", {"start": v(7.06, 0.5) * mm, "end": v(7.06, -0.55) * mm});
            skLineSegment(sketch, "E371", {"start": v(7.06, -0.55) * mm, "end": v(4.07, -0.55) * mm});
            skLineSegment(sketch, "E372", {"start": v(4.07, -0.55) * mm, "end": v(4.07, -0.93) * mm});
            skLineSegment(sketch, "E373", {"start": v(4.07, -0.93) * mm, "end": v(4.08, -1.08) * mm});
            skLineSegment(sketch, "E374", {"start": v(4.08, -1.08) * mm, "end": v(4.1, -1.2) * mm});
            skLineSegment(sketch, "E375", {"start": v(4.1, -1.2) * mm, "end": v(4.14, -1.3) * mm});
            skLineSegment(sketch, "E376", {"start": v(4.14, -1.3) * mm, "end": v(4.2, -1.38) * mm});
            skLineSegment(sketch, "E377", {"start": v(4.2, -1.38) * mm, "end": v(4.27, -1.44) * mm});
            skLineSegment(sketch, "E378", {"start": v(4.27, -1.44) * mm, "end": v(4.37, -1.48) * mm});
            skLineSegment(sketch, "E379", {"start": v(4.37, -1.48) * mm, "end": v(4.5, -1.5) * mm});
            skLineSegment(sketch, "E380", {"start": v(4.5, -1.5) * mm, "end": v(4.65, -1.5) * mm});
            skLineSegment(sketch, "E381", {"start": v(4.65, -1.5) * mm, "end": v(7.06, -1.5) * mm});
            skLineSegment(sketch, "E382", {"start": v(7.06, -1.5) * mm, "end": v(7.06, -2.57) * mm});
            skLineSegment(sketch, "E383", {"start": v(7.06, -2.57) * mm, "end": v(4.57, -2.57) * mm});
            skLineSegment(sketch, "E384", {"start": v(4.57, -2.57) * mm, "end": v(4.37, -2.56) * mm});
            skLineSegment(sketch, "E385", {"start": v(4.37, -2.56) * mm, "end": v(4.18, -2.54) * mm});
            skLineSegment(sketch, "E386", {"start": v(4.18, -2.54) * mm, "end": v(4, -2.52) * mm});
            skLineSegment(sketch, "E387", {"start": v(4, -2.52) * mm, "end": v(3.84, -2.48) * mm});
            skLineSegment(sketch, "E388", {"start": v(3.84, -2.48) * mm, "end": v(3.7, -2.43) * mm});
            skLineSegment(sketch, "E389", {"start": v(3.7, -2.43) * mm, "end": v(3.57, -2.36) * mm});
            skLineSegment(sketch, "E390", {"start": v(3.57, -2.36) * mm, "end": v(3.46, -2.29) * mm});
            skLineSegment(sketch, "E391", {"start": v(3.46, -2.29) * mm, "end": v(3.36, -2.2) * mm});
            skLineSegment(sketch, "E392", {"start": v(3.36, -2.2) * mm, "end": v(3.28, -2.1) * mm});
            skLineSegment(sketch, "E393", {"start": v(3.28, -2.1) * mm, "end": v(3.2, -2) * mm});
            skLineSegment(sketch, "E394", {"start": v(3.2, -2) * mm, "end": v(3.14, -1.86) * mm});
            skLineSegment(sketch, "E395", {"start": v(3.14, -1.86) * mm, "end": v(3.09, -1.72) * mm});
            skLineSegment(sketch, "E396", {"start": v(3.09, -1.72) * mm, "end": v(3.05, -1.56) * mm});
            skLineSegment(sketch, "E397", {"start": v(3.05, -1.56) * mm, "end": v(3.02, -1.38) * mm});
            skLineSegment(sketch, "E398", {"start": v(3.02, -1.38) * mm, "end": v(3, -1.2) * mm});
            skLineSegment(sketch, "E399", {"start": v(3, -1.2) * mm, "end": v(3, -0.99) * mm});
            skLineSegment(sketch, "E400", {"start": v(3, -0.99) * mm, "end": v(3, 0.9) * mm});
            skLineSegment(sketch, "E401", {"start": v(3, 0.9) * mm, "end": v(3, 1.1) * mm});
            skLineSegment(sketch, "E402", {"start": v(3, 1.1) * mm, "end": v(3.02, 1.29) * mm});
            skLineSegment(sketch, "E403", {"start": v(3.02, 1.29) * mm, "end": v(3.05, 1.46) * mm});
            skLineSegment(sketch, "E404", {"start": v(3.05, 1.46) * mm, "end": v(3.09, 1.62) * mm});
            skLineSegment(sketch, "E405", {"start": v(3.09, 1.62) * mm, "end": v(3.14, 1.77) * mm});
            skLineSegment(sketch, "E406", {"start": v(3.14, 1.77) * mm, "end": v(3.2, 1.9) * mm});
            skLineSegment(sketch, "E407", {"start": v(3.2, 1.9) * mm, "end": v(3.27, 2) * mm});
            skLineSegment(sketch, "E408", {"start": v(3.27, 2) * mm, "end": v(3.36, 2.1) * mm});
            skLineSegment(sketch, "E409", {"start": v(3.36, 2.1) * mm, "end": v(3.46, 2.2) * mm});
            skLineSegment(sketch, "E410", {"start": v(3.46, 2.2) * mm, "end": v(3.57, 2.26) * mm});
            skLineSegment(sketch, "E411", {"start": v(3.57, 2.26) * mm, "end": v(3.7, 2.33) * mm});
            skLineSegment(sketch, "E412", {"start": v(3.7, 2.33) * mm, "end": v(3.84, 2.38) * mm});
            skLineSegment(sketch, "E413", {"start": v(3.84, 2.38) * mm, "end": v(4, 2.42) * mm});
            skLineSegment(sketch, "E414", {"start": v(4, 2.42) * mm, "end": v(4.18, 2.44) * mm});
            skLineSegment(sketch, "E415", {"start": v(4.18, 2.44) * mm, "end": v(4.37, 2.46) * mm});
            skLineSegment(sketch, "E416", {"start": v(4.37, 2.46) * mm, "end": v(4.57, 2.47) * mm});
            skLineSegment(sketch, "E417", {"start": v(7.73, -0.28) * mm, "end": v(9.68, -0.28) * mm});
            skLineSegment(sketch, "E418", {"start": v(9.68, -0.28) * mm, "end": v(9.68, -1.21) * mm});
            skLineSegment(sketch, "E419", {"start": v(9.68, -1.21) * mm, "end": v(7.73, -1.21) * mm});
            skLineSegment(sketch, "E420", {"start": v(7.73, -1.21) * mm, "end": v(7.73, -0.28) * mm});
            skLineSegment(sketch, "E421", {"start": v(13.56, 1.64) * mm, "end": v(14.95, -2.57) * mm});
            skLineSegment(sketch, "E422", {"start": v(14.95, -2.57) * mm, "end": v(13.81, -2.57) * mm});
            skLineSegment(sketch, "E423", {"start": v(13.81, -2.57) * mm, "end": v(12.55, 1.33) * mm});
            skLineSegment(sketch, "E424", {"start": v(12.55, 1.33) * mm, "end": v(12.48, 1.47) * mm});
            skLineSegment(sketch, "E425", {"start": v(12.48, 1.47) * mm, "end": v(12.35, 1.5) * mm});
            skLineSegment(sketch, "E426", {"start": v(12.35, 1.5) * mm, "end": v(12.24, 1.47) * mm});
            skLineSegment(sketch, "E427", {"start": v(12.24, 1.47) * mm, "end": v(12.17, 1.33) * mm});
            skLineSegment(sketch, "E428", {"start": v(12.17, 1.33) * mm, "end": v(10.9, -2.57) * mm});
            skLineSegment(sketch, "E429", {"start": v(10.9, -2.57) * mm, "end": v(9.77, -2.57) * mm});
            skLineSegment(sketch, "E430", {"start": v(9.77, -2.57) * mm, "end": v(11.15, 1.64) * mm});
            skLineSegment(sketch, "E431", {"start": v(11.15, 1.64) * mm, "end": v(11.24, 1.87) * mm});
            skLineSegment(sketch, "E432", {"start": v(11.24, 1.87) * mm, "end": v(11.34, 2.06) * mm});
            skLineSegment(sketch, "E433", {"start": v(11.34, 2.06) * mm, "end": v(11.46, 2.22) * mm});
            skLineSegment(sketch, "E434", {"start": v(11.46, 2.22) * mm, "end": v(11.6, 2.35) * mm});
            skLineSegment(sketch, "E435", {"start": v(11.6, 2.35) * mm, "end": v(11.75, 2.44) * mm});
            skLineSegment(sketch, "E436", {"start": v(11.75, 2.44) * mm, "end": v(11.93, 2.51) * mm});
            skLineSegment(sketch, "E437", {"start": v(11.93, 2.51) * mm, "end": v(12.13, 2.55) * mm});
            skLineSegment(sketch, "E438", {"start": v(12.13, 2.55) * mm, "end": v(12.35, 2.57) * mm});
            skLineSegment(sketch, "E439", {"start": v(12.35, 2.57) * mm, "end": v(12.58, 2.55) * mm});
            skLineSegment(sketch, "E440", {"start": v(12.58, 2.55) * mm, "end": v(12.78, 2.5) * mm});
            skLineSegment(sketch, "E441", {"start": v(12.78, 2.5) * mm, "end": v(12.96, 2.44) * mm});
            skLineSegment(sketch, "E442", {"start": v(12.96, 2.44) * mm, "end": v(13.12, 2.33) * mm});
            skLineSegment(sketch, "E443", {"start": v(13.12, 2.33) * mm, "end": v(13.26, 2.2) * mm});
            skLineSegment(sketch, "E444", {"start": v(13.26, 2.2) * mm, "end": v(13.38, 2.04) * mm});
            skLineSegment(sketch, "E445", {"start": v(13.38, 2.04) * mm, "end": v(13.48, 1.86) * mm});
            skLineSegment(sketch, "E446", {"start": v(13.48, 1.86) * mm, "end": v(13.56, 1.64) * mm});
            skLineSegment(sketch, "E447", {"start": v(15.04, -0.28) * mm, "end": v(16.98, -0.28) * mm});
            skLineSegment(sketch, "E448", {"start": v(16.98, -0.28) * mm, "end": v(16.98, -1.21) * mm});
            skLineSegment(sketch, "E449", {"start": v(16.98, -1.21) * mm, "end": v(15.04, -1.21) * mm});
            skLineSegment(sketch, "E450", {"start": v(15.04, -1.21) * mm, "end": v(15.04, -0.28) * mm});
            skLineSegment(sketch, "E451", {"start": v(17.69, 2.47) * mm, "end": v(18.76, 2.47) * mm});
            skLineSegment(sketch, "E452", {"start": v(18.76, 2.47) * mm, "end": v(18.76, -0.93) * mm});
            skLineSegment(sketch, "E453", {"start": v(18.76, -0.93) * mm, "end": v(18.77, -1.08) * mm});
            skLineSegment(sketch, "E454", {"start": v(18.77, -1.08) * mm, "end": v(18.8, -1.2) * mm});
            skLineSegment(sketch, "E455", {"start": v(18.8, -1.2) * mm, "end": v(18.83, -1.3) * mm});
            skLineSegment(sketch, "E456", {"start": v(18.83, -1.3) * mm, "end": v(18.89, -1.38) * mm});
            skLineSegment(sketch, "E457", {"start": v(18.89, -1.38) * mm, "end": v(18.96, -1.44) * mm});
            skLineSegment(sketch, "E458", {"start": v(18.96, -1.44) * mm, "end": v(19.07, -1.48) * mm});
            skLineSegment(sketch, "E459", {"start": v(19.07, -1.48) * mm, "end": v(19.2, -1.5) * mm});
            skLineSegment(sketch, "E460", {"start": v(19.2, -1.5) * mm, "end": v(19.35, -1.5) * mm});
            skLineSegment(sketch, "E461", {"start": v(19.35, -1.5) * mm, "end": v(20.98, -1.5) * mm});
            skLineSegment(sketch, "E462", {"start": v(20.98, -1.5) * mm, "end": v(20.98, -2.57) * mm});
            skLineSegment(sketch, "E463", {"start": v(20.98, -2.57) * mm, "end": v(19.27, -2.57) * mm});
            skLineSegment(sketch, "E464", {"start": v(19.27, -2.57) * mm, "end": v(19.06, -2.56) * mm});
            skLineSegment(sketch, "E465", {"start": v(19.06, -2.56) * mm, "end": v(18.87, -2.54) * mm});
            skLineSegment(sketch, "E466", {"start": v(18.87, -2.54) * mm, "end": v(18.7, -2.52) * mm});
            skLineSegment(sketch, "E467", {"start": v(18.7, -2.52) * mm, "end": v(18.54, -2.48) * mm});
            skLineSegment(sketch, "E468", {"start": v(18.54, -2.48) * mm, "end": v(18.4, -2.43) * mm});
            skLineSegment(sketch, "E469", {"start": v(18.4, -2.43) * mm, "end": v(18.27, -2.36) * mm});
            skLineSegment(sketch, "E470", {"start": v(18.27, -2.36) * mm, "end": v(18.15, -2.29) * mm});
            skLineSegment(sketch, "E471", {"start": v(18.15, -2.29) * mm, "end": v(18.05, -2.2) * mm});
            skLineSegment(sketch, "E472", {"start": v(18.05, -2.2) * mm, "end": v(17.97, -2.1) * mm});
            skLineSegment(sketch, "E473", {"start": v(17.97, -2.1) * mm, "end": v(17.9, -2) * mm});
            skLineSegment(sketch, "E474", {"start": v(17.9, -2) * mm, "end": v(17.83, -1.86) * mm});
            skLineSegment(sketch, "E475", {"start": v(17.83, -1.86) * mm, "end": v(17.78, -1.72) * mm});
            skLineSegment(sketch, "E476", {"start": v(17.78, -1.72) * mm, "end": v(17.74, -1.56) * mm});
            skLineSegment(sketch, "E477", {"start": v(17.74, -1.56) * mm, "end": v(17.71, -1.38) * mm});
            skLineSegment(sketch, "E478", {"start": v(17.71, -1.38) * mm, "end": v(17.7, -1.2) * mm});
            skLineSegment(sketch, "E479", {"start": v(17.7, -1.2) * mm, "end": v(17.69, -0.99) * mm});
            skLineSegment(sketch, "E480", {"start": v(17.69, -0.99) * mm, "end": v(17.69, 2.47) * mm});
            skLineSegment(sketch, "E481", {"start": v(24.55, 1.64) * mm, "end": v(25.95, -2.57) * mm});
            skLineSegment(sketch, "E482", {"start": v(25.95, -2.57) * mm, "end": v(24.8, -2.57) * mm});
            skLineSegment(sketch, "E483", {"start": v(24.8, -2.57) * mm, "end": v(23.55, 1.33) * mm});
            skLineSegment(sketch, "E484", {"start": v(23.55, 1.33) * mm, "end": v(23.47, 1.47) * mm});
            skLineSegment(sketch, "E485", {"start": v(23.47, 1.47) * mm, "end": v(23.35, 1.5) * mm});
            skLineSegment(sketch, "E486", {"start": v(23.35, 1.5) * mm, "end": v(23.23, 1.47) * mm});
            skLineSegment(sketch, "E487", {"start": v(23.23, 1.47) * mm, "end": v(23.16, 1.33) * mm});
            skLineSegment(sketch, "E488", {"start": v(23.16, 1.33) * mm, "end": v(21.9, -2.57) * mm});
            skLineSegment(sketch, "E489", {"start": v(21.9, -2.57) * mm, "end": v(20.76, -2.57) * mm});
            skLineSegment(sketch, "E490", {"start": v(20.76, -2.57) * mm, "end": v(22.14, 1.64) * mm});
            skLineSegment(sketch, "E491", {"start": v(22.14, 1.64) * mm, "end": v(22.23, 1.87) * mm});
            skLineSegment(sketch, "E492", {"start": v(22.23, 1.87) * mm, "end": v(22.34, 2.06) * mm});
            skLineSegment(sketch, "E493", {"start": v(22.34, 2.06) * mm, "end": v(22.46, 2.22) * mm});
            skLineSegment(sketch, "E494", {"start": v(22.46, 2.22) * mm, "end": v(22.6, 2.35) * mm});
            skLineSegment(sketch, "E495", {"start": v(22.6, 2.35) * mm, "end": v(22.75, 2.44) * mm});
            skLineSegment(sketch, "E496", {"start": v(22.75, 2.44) * mm, "end": v(22.92, 2.51) * mm});
            skLineSegment(sketch, "E497", {"start": v(22.92, 2.51) * mm, "end": v(23.13, 2.55) * mm});
            skLineSegment(sketch, "E498", {"start": v(23.13, 2.55) * mm, "end": v(23.35, 2.57) * mm});
            skLineSegment(sketch, "E499", {"start": v(23.35, 2.57) * mm, "end": v(23.57, 2.55) * mm});
            skLineSegment(sketch, "E500", {"start": v(23.57, 2.55) * mm, "end": v(23.78, 2.5) * mm});
            skLineSegment(sketch, "E501", {"start": v(23.78, 2.5) * mm, "end": v(23.96, 2.44) * mm});
            skLineSegment(sketch, "E502", {"start": v(23.96, 2.44) * mm, "end": v(24.12, 2.33) * mm});
            skLineSegment(sketch, "E503", {"start": v(24.12, 2.33) * mm, "end": v(24.26, 2.2) * mm});
            skLineSegment(sketch, "E504", {"start": v(24.26, 2.2) * mm, "end": v(24.38, 2.04) * mm});
            skLineSegment(sketch, "E505", {"start": v(24.38, 2.04) * mm, "end": v(24.48, 1.86) * mm});
            skLineSegment(sketch, "E506", {"start": v(24.48, 1.86) * mm, "end": v(24.55, 1.64) * mm});
            skLineSegment(sketch, "E507", {"start": v(27.63, 2.47) * mm, "end": v(30.24, 2.47) * mm});
            skLineSegment(sketch, "E508", {"start": v(30.24, 2.47) * mm, "end": v(30.24, 1.41) * mm});
            skLineSegment(sketch, "E509", {"start": v(30.24, 1.41) * mm, "end": v(27.61, 1.41) * mm});
            skLineSegment(sketch, "E510", {"start": v(27.61, 1.41) * mm, "end": v(27.49, 1.4) * mm});
            skLineSegment(sketch, "E511", {"start": v(27.49, 1.4) * mm, "end": v(27.38, 1.39) * mm});
            skLineSegment(sketch, "E512", {"start": v(27.38, 1.39) * mm, "end": v(27.29, 1.35) * mm});
            skLineSegment(sketch, "E513", {"start": v(27.29, 1.35) * mm, "end": v(27.21, 1.3) * mm});
            skLineSegment(sketch, "E514", {"start": v(27.21, 1.3) * mm, "end": v(27.15, 1.23) * mm});
            skLineSegment(sketch, "E515", {"start": v(27.15, 1.23) * mm, "end": v(27.1, 1.16) * mm});
            skLineSegment(sketch, "E516", {"start": v(27.1, 1.16) * mm, "end": v(27.08, 1.06) * mm});
            skLineSegment(sketch, "E517", {"start": v(27.08, 1.06) * mm, "end": v(27.07, 0.96) * mm});
            skLineSegment(sketch, "E518", {"start": v(27.07, 0.96) * mm, "end": v(27.08, 0.85) * mm});
            skLineSegment(sketch, "E519", {"start": v(27.08, 0.85) * mm, "end": v(27.1, 0.76) * mm});
            skLineSegment(sketch, "E520", {"start": v(27.1, 0.76) * mm, "end": v(27.15, 0.68) * mm});
            skLineSegment(sketch, "E521", {"start": v(27.15, 0.68) * mm, "end": v(27.21, 0.62) * mm});
            skLineSegment(sketch, "E522", {"start": v(27.21, 0.62) * mm, "end": v(27.29, 0.57) * mm});
            skLineSegment(sketch, "E523", {"start": v(27.29, 0.57) * mm, "end": v(27.38, 0.54) * mm});
            skLineSegment(sketch, "E524", {"start": v(27.38, 0.54) * mm, "end": v(27.49, 0.51) * mm});
            skLineSegment(sketch, "E525", {"start": v(27.49, 0.51) * mm, "end": v(27.61, 0.5) * mm});
            skLineSegment(sketch, "E526", {"start": v(27.61, 0.5) * mm, "end": v(28.74, 0.5) * mm});
            skLineSegment(sketch, "E527", {"start": v(28.74, 0.5) * mm, "end": v(28.94, 0.5) * mm});
            skLineSegment(sketch, "E528", {"start": v(28.94, 0.5) * mm, "end": v(29.12, 0.48) * mm});
            skLineSegment(sketch, "E529", {"start": v(29.12, 0.48) * mm, "end": v(29.3, 0.45) * mm});
            skLineSegment(sketch, "E530", {"start": v(29.3, 0.45) * mm, "end": v(29.47, 0.4) * mm});
            skLineSegment(sketch, "E531", {"start": v(29.47, 0.4) * mm, "end": v(29.62, 0.35) * mm});
            skLineSegment(sketch, "E532", {"start": v(29.62, 0.35) * mm, "end": v(29.76, 0.28) * mm});
            skLineSegment(sketch, "E533", {"start": v(29.76, 0.28) * mm, "end": v(29.9, 0.2) * mm});
            skLineSegment(sketch, "E534", {"start": v(29.9, 0.2) * mm, "end": v(30.01, 0.1) * mm});
            skLineSegment(sketch, "E535", {"start": v(30.01, 0.1) * mm, "end": v(30.12, 0) * mm});
            skLineSegment(sketch, "E536", {"start": v(30.12, 0) * mm, "end": v(30.21, -0.12) * mm});
            skLineSegment(sketch, "E537", {"start": v(30.21, -0.12) * mm, "end": v(30.29, -0.25) * mm});
            skLineSegment(sketch, "E538", {"start": v(30.29, -0.25) * mm, "end": v(30.35, -0.39) * mm});
            skLineSegment(sketch, "E539", {"start": v(30.35, -0.39) * mm, "end": v(30.4, -0.53) * mm});
            skLineSegment(sketch, "E540", {"start": v(30.4, -0.53) * mm, "end": v(30.44, -0.69) * mm});
            skLineSegment(sketch, "E541", {"start": v(30.44, -0.69) * mm, "end": v(30.46, -0.85) * mm});
            skLineSegment(sketch, "E542", {"start": v(30.46, -0.85) * mm, "end": v(30.47, -1.03) * mm});
            skLineSegment(sketch, "E543", {"start": v(30.47, -1.03) * mm, "end": v(30.46, -1.2) * mm});
            skLineSegment(sketch, "E544", {"start": v(30.46, -1.2) * mm, "end": v(30.44, -1.37) * mm});
            skLineSegment(sketch, "E545", {"start": v(30.44, -1.37) * mm, "end": v(30.4, -1.53) * mm});
            skLineSegment(sketch, "E546", {"start": v(30.4, -1.53) * mm, "end": v(30.35, -1.67) * mm});
            skLineSegment(sketch, "E547", {"start": v(30.35, -1.67) * mm, "end": v(30.29, -1.8) * mm});
            skLineSegment(sketch, "E548", {"start": v(30.29, -1.8) * mm, "end": v(30.21, -1.94) * mm});
            skLineSegment(sketch, "E549", {"start": v(30.21, -1.94) * mm, "end": v(30.12, -2.05) * mm});
            skLineSegment(sketch, "E550", {"start": v(30.12, -2.05) * mm, "end": v(30.01, -2.16) * mm});
            skLineSegment(sketch, "E551", {"start": v(30.01, -2.16) * mm, "end": v(29.9, -2.26) * mm});
            skLineSegment(sketch, "E552", {"start": v(29.9, -2.26) * mm, "end": v(29.76, -2.34) * mm});
            skLineSegment(sketch, "E553", {"start": v(29.76, -2.34) * mm, "end": v(29.62, -2.4) * mm});
            skLineSegment(sketch, "E554", {"start": v(29.62, -2.4) * mm, "end": v(29.47, -2.47) * mm});
            skLineSegment(sketch, "E555", {"start": v(29.47, -2.47) * mm, "end": v(29.3, -2.5) * mm});
            skLineSegment(sketch, "E556", {"start": v(29.3, -2.5) * mm, "end": v(29.12, -2.54) * mm});
            skLineSegment(sketch, "E557", {"start": v(29.12, -2.54) * mm, "end": v(28.94, -2.56) * mm});
            skLineSegment(sketch, "E558", {"start": v(28.94, -2.56) * mm, "end": v(28.74, -2.57) * mm});
            skLineSegment(sketch, "E559", {"start": v(28.74, -2.57) * mm, "end": v(26.1, -2.57) * mm});
            skLineSegment(sketch, "E560", {"start": v(26.1, -2.57) * mm, "end": v(26.1, -1.5) * mm});
            skLineSegment(sketch, "E561", {"start": v(26.1, -1.5) * mm, "end": v(28.77, -1.5) * mm});
            skLineSegment(sketch, "E562", {"start": v(28.77, -1.5) * mm, "end": v(28.9, -1.5) * mm});
            skLineSegment(sketch, "E563", {"start": v(28.9, -1.5) * mm, "end": v(29.04, -1.48) * mm});
            skLineSegment(sketch, "E564", {"start": v(29.04, -1.48) * mm, "end": v(29.14, -1.44) * mm});
            skLineSegment(sketch, "E565", {"start": v(29.14, -1.44) * mm, "end": v(29.23, -1.39) * mm});
            skLineSegment(sketch, "E566", {"start": v(29.23, -1.39) * mm, "end": v(29.3, -1.32) * mm});
            skLineSegment(sketch, "E567", {"start": v(29.3, -1.32) * mm, "end": v(29.35, -1.24) * mm});
            skLineSegment(sketch, "E568", {"start": v(29.35, -1.24) * mm, "end": v(29.38, -1.14) * mm});
            skLineSegment(sketch, "E569", {"start": v(29.38, -1.14) * mm, "end": v(29.39, -1.03) * mm});
            skLineSegment(sketch, "E570", {"start": v(29.39, -1.03) * mm, "end": v(29.38, -0.92) * mm});
            skLineSegment(sketch, "E571", {"start": v(29.38, -0.92) * mm, "end": v(29.35, -0.82) * mm});
            skLineSegment(sketch, "E572", {"start": v(29.35, -0.82) * mm, "end": v(29.3, -0.74) * mm});
            skLineSegment(sketch, "E573", {"start": v(29.3, -0.74) * mm, "end": v(29.23, -0.67) * mm});
            skLineSegment(sketch, "E574", {"start": v(29.23, -0.67) * mm, "end": v(29.14, -0.62) * mm});
            skLineSegment(sketch, "E575", {"start": v(29.14, -0.62) * mm, "end": v(29.04, -0.58) * mm});
            skLineSegment(sketch, "E576", {"start": v(29.04, -0.58) * mm, "end": v(28.9, -0.56) * mm});
            skLineSegment(sketch, "E577", {"start": v(28.9, -0.56) * mm, "end": v(28.77, -0.55) * mm});
            skLineSegment(sketch, "E578", {"start": v(28.77, -0.55) * mm, "end": v(27.63, -0.55) * mm});
            skLineSegment(sketch, "E579", {"start": v(27.63, -0.55) * mm, "end": v(27.45, -0.54) * mm});
            skLineSegment(sketch, "E580", {"start": v(27.45, -0.54) * mm, "end": v(27.27, -0.53) * mm});
            skLineSegment(sketch, "E581", {"start": v(27.27, -0.53) * mm, "end": v(27.11, -0.5) * mm});
            skLineSegment(sketch, "E582", {"start": v(27.11, -0.5) * mm, "end": v(26.96, -0.45) * mm});
            skLineSegment(sketch, "E583", {"start": v(26.96, -0.45) * mm, "end": v(26.81, -0.4) * mm});
            skLineSegment(sketch, "E584", {"start": v(26.81, -0.4) * mm, "end": v(26.68, -0.32) * mm});
            skLineSegment(sketch, "E585", {"start": v(26.68, -0.32) * mm, "end": v(26.55, -0.24) * mm});
            skLineSegment(sketch, "E586", {"start": v(26.55, -0.24) * mm, "end": v(26.44, -0.15) * mm});
            skLineSegment(sketch, "E587", {"start": v(26.44, -0.15) * mm, "end": v(26.34, -0.04) * mm});
            skLineSegment(sketch, "E588", {"start": v(26.34, -0.04) * mm, "end": v(26.25, 0.08) * mm});
            skLineSegment(sketch, "E589", {"start": v(26.25, 0.08) * mm, "end": v(26.17, 0.2) * mm});
            skLineSegment(sketch, "E590", {"start": v(26.17, 0.2) * mm, "end": v(26.11, 0.33) * mm});
            skLineSegment(sketch, "E591", {"start": v(26.11, 0.33) * mm, "end": v(26.06, 0.48) * mm});
            skLineSegment(sketch, "E592", {"start": v(26.06, 0.48) * mm, "end": v(26.03, 0.63) * mm});
            skLineSegment(sketch, "E593", {"start": v(26.03, 0.63) * mm, "end": v(26, 0.79) * mm});
            skLineSegment(sketch, "E594", {"start": v(26, 0.79) * mm, "end": v(26, 0.96) * mm});
            skLineSegment(sketch, "E595", {"start": v(26, 0.96) * mm, "end": v(26, 1.13) * mm});
            skLineSegment(sketch, "E596", {"start": v(26, 1.13) * mm, "end": v(26.03, 1.29) * mm});
            skLineSegment(sketch, "E597", {"start": v(26.03, 1.29) * mm, "end": v(26.06, 1.44) * mm});
            skLineSegment(sketch, "E598", {"start": v(26.06, 1.44) * mm, "end": v(26.11, 1.58) * mm});
            skLineSegment(sketch, "E599", {"start": v(26.11, 1.58) * mm, "end": v(26.17, 1.72) * mm});
            skLineSegment(sketch, "E600", {"start": v(26.17, 1.72) * mm, "end": v(26.25, 1.84) * mm});
            skLineSegment(sketch, "E601", {"start": v(26.25, 1.84) * mm, "end": v(26.34, 1.96) * mm});
            skLineSegment(sketch, "E602", {"start": v(26.34, 1.96) * mm, "end": v(26.44, 2.06) * mm});
            skLineSegment(sketch, "E603", {"start": v(26.44, 2.06) * mm, "end": v(26.55, 2.16) * mm});
            skLineSegment(sketch, "E604", {"start": v(26.55, 2.16) * mm, "end": v(26.68, 2.24) * mm});
            skLineSegment(sketch, "E605", {"start": v(26.68, 2.24) * mm, "end": v(26.81, 2.3) * mm});
            skLineSegment(sketch, "E606", {"start": v(26.81, 2.3) * mm, "end": v(26.96, 2.36) * mm});
            skLineSegment(sketch, "E607", {"start": v(26.96, 2.36) * mm, "end": v(27.11, 2.4) * mm});
            skLineSegment(sketch, "E608", {"start": v(27.11, 2.4) * mm, "end": v(27.27, 2.44) * mm});
            skLineSegment(sketch, "E609", {"start": v(27.27, 2.44) * mm, "end": v(27.45, 2.46) * mm});
            skLineSegment(sketch, "E610", {"start": v(27.45, 2.46) * mm, "end": v(27.63, 2.47) * mm});
            skLineSegment(sketch, "E611", {"start": v(32.51, 2.47) * mm, "end": v(35, 2.47) * mm});
            skLineSegment(sketch, "E612", {"start": v(35, 2.47) * mm, "end": v(35, 1.41) * mm});
            skLineSegment(sketch, "E613", {"start": v(35, 1.41) * mm, "end": v(32.6, 1.41) * mm});
            skLineSegment(sketch, "E614", {"start": v(32.6, 1.41) * mm, "end": v(32.44, 1.4) * mm});
            skLineSegment(sketch, "E615", {"start": v(32.44, 1.4) * mm, "end": v(32.31, 1.38) * mm});
            skLineSegment(sketch, "E616", {"start": v(32.31, 1.38) * mm, "end": v(32.21, 1.34) * mm});
            skLineSegment(sketch, "E617", {"start": v(32.21, 1.34) * mm, "end": v(32.14, 1.29) * mm});
            skLineSegment(sketch, "E618", {"start": v(32.14, 1.29) * mm, "end": v(32.08, 1.21) * mm});
            skLineSegment(sketch, "E619", {"start": v(32.08, 1.21) * mm, "end": v(32.04, 1.11) * mm});
            skLineSegment(sketch, "E620", {"start": v(32.04, 1.11) * mm, "end": v(32.02, 0.98) * mm});
            skLineSegment(sketch, "E621", {"start": v(32.02, 0.98) * mm, "end": v(32.01, 0.83) * mm});
            skLineSegment(sketch, "E622", {"start": v(32.01, 0.83) * mm, "end": v(32.01, 0.5) * mm});
            skLineSegment(sketch, "E623", {"start": v(32.01, 0.5) * mm, "end": v(35, 0.5) * mm});
            skLineSegment(sketch, "E624", {"start": v(35, 0.5) * mm, "end": v(35, -0.55) * mm});
            skLineSegment(sketch, "E625", {"start": v(35, -0.55) * mm, "end": v(32.01, -0.55) * mm});
            skLineSegment(sketch, "E626", {"start": v(32.01, -0.55) * mm, "end": v(32.01, -0.93) * mm});
            skLineSegment(sketch, "E627", {"start": v(32.01, -0.93) * mm, "end": v(32.02, -1.08) * mm});
            skLineSegment(sketch, "E628", {"start": v(32.02, -1.08) * mm, "end": v(32.04, -1.2) * mm});
            skLineSegment(sketch, "E629", {"start": v(32.04, -1.2) * mm, "end": v(32.08, -1.3) * mm});
            skLineSegment(sketch, "E630", {"start": v(32.08, -1.3) * mm, "end": v(32.14, -1.38) * mm});
            skLineSegment(sketch, "E631", {"start": v(32.14, -1.38) * mm, "end": v(32.21, -1.44) * mm});
            skLineSegment(sketch, "E632", {"start": v(32.21, -1.44) * mm, "end": v(32.31, -1.48) * mm});
            skLineSegment(sketch, "E633", {"start": v(32.31, -1.48) * mm, "end": v(32.44, -1.5) * mm});
            skLineSegment(sketch, "E634", {"start": v(32.44, -1.5) * mm, "end": v(32.6, -1.5) * mm});
            skLineSegment(sketch, "E635", {"start": v(32.6, -1.5) * mm, "end": v(35, -1.5) * mm});
            skLineSegment(sketch, "E636", {"start": v(35, -1.5) * mm, "end": v(35, -2.57) * mm});
            skLineSegment(sketch, "E637", {"start": v(35, -2.57) * mm, "end": v(32.51, -2.57) * mm});
            skLineSegment(sketch, "E638", {"start": v(32.51, -2.57) * mm, "end": v(32.3, -2.56) * mm});
            skLineSegment(sketch, "E639", {"start": v(32.3, -2.56) * mm, "end": v(32.12, -2.54) * mm});
            skLineSegment(sketch, "E640", {"start": v(32.12, -2.54) * mm, "end": v(31.94, -2.52) * mm});
            skLineSegment(sketch, "E641", {"start": v(31.94, -2.52) * mm, "end": v(31.78, -2.48) * mm});
            skLineSegment(sketch, "E642", {"start": v(31.78, -2.48) * mm, "end": v(31.64, -2.43) * mm});
            skLineSegment(sketch, "E643", {"start": v(31.64, -2.43) * mm, "end": v(31.51, -2.36) * mm});
            skLineSegment(sketch, "E644", {"start": v(31.51, -2.36) * mm, "end": v(31.4, -2.29) * mm});
            skLineSegment(sketch, "E645", {"start": v(31.4, -2.29) * mm, "end": v(31.3, -2.2) * mm});
            skLineSegment(sketch, "E646", {"start": v(31.3, -2.2) * mm, "end": v(31.22, -2.1) * mm});
            skLineSegment(sketch, "E647", {"start": v(31.22, -2.1) * mm, "end": v(31.14, -2) * mm});
            skLineSegment(sketch, "E648", {"start": v(31.14, -2) * mm, "end": v(31.08, -1.86) * mm});
            skLineSegment(sketch, "E649", {"start": v(31.08, -1.86) * mm, "end": v(31.03, -1.72) * mm});
            skLineSegment(sketch, "E650", {"start": v(31.03, -1.72) * mm, "end": v(31, -1.56) * mm});
            skLineSegment(sketch, "E651", {"start": v(31, -1.56) * mm, "end": v(30.96, -1.38) * mm});
            skLineSegment(sketch, "E652", {"start": v(30.96, -1.38) * mm, "end": v(30.95, -1.2) * mm});
            skLineSegment(sketch, "E653", {"start": v(30.95, -1.2) * mm, "end": v(30.94, -0.99) * mm});
            skLineSegment(sketch, "E654", {"start": v(30.94, -0.99) * mm, "end": v(30.94, 0.9) * mm});
            skLineSegment(sketch, "E655", {"start": v(30.94, 0.9) * mm, "end": v(30.95, 1.1) * mm});
            skLineSegment(sketch, "E656", {"start": v(30.95, 1.1) * mm, "end": v(30.96, 1.29) * mm});
            skLineSegment(sketch, "E657", {"start": v(30.96, 1.29) * mm, "end": v(30.99, 1.46) * mm});
            skLineSegment(sketch, "E658", {"start": v(30.99, 1.46) * mm, "end": v(31.03, 1.62) * mm});
            skLineSegment(sketch, "E659", {"start": v(31.03, 1.62) * mm, "end": v(31.08, 1.77) * mm});
            skLineSegment(sketch, "E660", {"start": v(31.08, 1.77) * mm, "end": v(31.14, 1.9) * mm});
            skLineSegment(sketch, "E661", {"start": v(31.14, 1.9) * mm, "end": v(31.21, 2) * mm});
            skLineSegment(sketch, "E662", {"start": v(31.21, 2) * mm, "end": v(31.3, 2.1) * mm});
            skLineSegment(sketch, "E663", {"start": v(31.3, 2.1) * mm, "end": v(31.4, 2.2) * mm});
            skLineSegment(sketch, "E664", {"start": v(31.4, 2.2) * mm, "end": v(31.5, 2.26) * mm});
            skLineSegment(sketch, "E665", {"start": v(31.5, 2.26) * mm, "end": v(31.64, 2.33) * mm});
            skLineSegment(sketch, "E666", {"start": v(31.64, 2.33) * mm, "end": v(31.78, 2.38) * mm});
            skLineSegment(sketch, "E667", {"start": v(31.78, 2.38) * mm, "end": v(31.94, 2.42) * mm});
            skLineSegment(sketch, "E668", {"start": v(31.94, 2.42) * mm, "end": v(32.12, 2.44) * mm});
            skLineSegment(sketch, "E669", {"start": v(32.12, 2.44) * mm, "end": v(32.3, 2.46) * mm});
            skLineSegment(sketch, "E670", {"start": v(32.3, 2.46) * mm, "end": v(32.51, 2.47) * mm});
            skSolve(sketch);
        }
        {
            var Q0;
            Q0=qSketchRegion(id+"F0",true);
            var Q1;
            Q1=makeQuery(id+"F0.imprint","IMPRINT",FACE,{"disambiguationData":[TD([[makeQuery(id+"F0.imprint","IMPRINT",EDGE,{"derivedFrom":sQuery(id+"F0.wireOp",EDGE,"E116")}),-1.0]])]});
            var Q2;
            Q2=makeQuery(id+"F0.imprint","IMPRINT",FACE,{"disambiguationData":[TD([[makeQuery(id+"F0.imprint","IMPRINT",EDGE,{"derivedFrom":sQuery(id+"F0.wireOp",EDGE,"E64")}),-1.0]])]});
            var Q3;
            Q3=makeQuery(id+"F0.imprint","IMPRINT",FACE,{"disambiguationData":[TD([[makeQuery(id+"F0.imprint","IMPRINT",EDGE,{"derivedFrom":sQuery(id+"F0.wireOp",EDGE,"E94")}),-1.0]])]});
            extrude(context, id + "F1", {"entities" : qUnion([Q0, Q1, Q2, Q3]), "depth" : 1 * mm});
        }
        {
            var Q0;
            Q0=qCreatedBy(makeId("Top.planeOp"),FACE);
            var sketch = newSketch(context, id + "F2", { "sketchPlane" : qUnion([Q0])});
            skLineSegment(sketch, "E671.bottom", {"start": v(47.5, -27.5) * mm, "end": v(-47.5, -27.5) * mm});
            skLineSegment(sketch, "E671.top", {"start": v(47.5, 27.5) * mm, "end": v(-47.5, 27.5) * mm});
            skLineSegment(sketch, "E671.left", {"start": v(52.5, -22.5) * mm, "end": v(52.5, 22.5) * mm});
            skLineSegment(sketch, "E671.right", {"start": v(-52.5, -22.5) * mm, "end": v(-52.5, 22.5) * mm});
            skPoint(sketch, "E671.middle", {"position": v(0, 0) * mm});
            skPoint(sketch, "E672.visualSharp", {"position": v(-52.5, 27.5) * mm});
            skArc(sketch, "E672.filletArc", {"start": v(-47.5, 27.5) * mm, "mid": v(-51.04, 26.04) * mm, "end": v(-52.5, 22.5) * mm});
            skPoint(sketch, "E673.visualSharp", {"position": v(52.5, 27.5) * mm});
            skArc(sketch, "E673.filletArc", {"start": v(52.5, 22.5) * mm, "mid": v(51.04, 26.04) * mm, "end": v(47.5, 27.5) * mm});
            skPoint(sketch, "E674.visualSharp", {"position": v(52.5, -27.5) * mm});
            skArc(sketch, "E674.filletArc", {"start": v(47.5, -27.5) * mm, "mid": v(51.04, -26.04) * mm, "end": v(52.5, -22.5) * mm});
            skPoint(sketch, "E675.visualSharp", {"position": v(-52.5, -27.5) * mm});
            skArc(sketch, "E675.filletArc", {"start": v(-52.5, -22.5) * mm, "mid": v(-51.04, -26.04) * mm, "end": v(-47.5, -27.5) * mm});
            skSolve(sketch);
        }
        {
            var Q0;
            Q0=makeQuery(id+"F2.imprint","IMPRINT",FACE,{"disambiguationData":[TD([[makeQuery(id+"F2.imprint","IMPRINT",EDGE,{"derivedFrom":sQuery(id+"F2.wireOp",EDGE,"E671.bottom")}),-1.0]])]});
            var sketch = newSketch(context, id + "F3", { "sketchPlane" : qUnion([Q0])});
            skText(sketch, "E676", { "text": "<email>\n       facebook.com/createalase\n", "fontName": "OpenSans-Bold.ttf"});
            const initialGuessF3  = {"E676": [-0.0375, -0.0155, 1, 0, 0.00314]};
            skSetInitialGuess(sketch, initialGuessF3);
            skSolve(sketch);
        }
        {
            var Q0;
            Q0=qSketchRegion(id+"F2",true);
            extrude(context, id + "F4", {"entities" : qUnion([Q0]), "operationType" : NewBodyOperationType.ADD, "oppositeDirection" : true, "depth" : 1 * mm, "offsetDistance" : 25 * mm});
        }
        {
            var Q0;
            Q0=qSketchRegion(id+"F3",true);
            extrude(context, id + "F5", {"entities" : qUnion([Q0]), "operationType" : NewBodyOperationType.REMOVE, "oppositeDirection" : true, "depth" : .5 * mm});
        }
        {
            var Q0;
            {var subQ6=sQuery(id+"F2.wireOp",EDGE,"E671.bottom");var subQ54=sQuery(id+"F2.wireOp",EDGE,"E672.filletArc");var subQ56=sQuery(id+"F2.wireOp",EDGE,"E671.right");var subQ59=sQuery(id+"F2.wireOp",EDGE,"E671.left");var subQ61=sQuery(id+"F2.wireOp",EDGE,"E671.top");var subQ357=sQuery(id+"F2.wireOp",EDGE,"E675.filletArc");var subQ406=sQuery(id+"F2.wireOp",EDGE,"E673.filletArc");var subQ529=sQuery(id+"F2.wireOp",EDGE,"E674.filletArc");var subQ559=makeQuery(id+"F1.opExtrude","SWEPT_FACE",FACE,{"disambiguationData":[OSD([sQuery(id+"F0.wireOp",EDGE,"E0")])]});Q0=makeQuery(id+"F5.boolean.opBoolean","SPLIT",FACE,{"disambiguationData":[TD([subQ559])],"derivedFrom":makeQuery(id+"F4.boolean.opBoolean","SPLIT",FACE,{"disambiguationData":[TD([subQ559])],"derivedFrom":makeQuery(id+"F4.opExtrude","CAP_FACE",FACE,{"disambiguationData":[OSD([subQ6,subQ61,subQ59,subQ56,subQ54,subQ406,subQ529,subQ357])],"isStart":true})})});}
            var sketch = newSketch(context, id + "F6", { "sketchPlane" : qUnion([Q0])});
            skText(sketch, "E677", { "text": "Making Stuff Personal", "fontName": "OpenSans-Bold.ttf"});
            const initialGuessF6  = {"E677": [-0.0375, 0.01458, 1, 0, 0.00492]};
            skSetInitialGuess(sketch, initialGuessF6);
            skSolve(sketch);
        }
        {
            var Q0;
            Q0=qSketchRegion(id+"F6",true);
            extrude(context, id + "F7", {"entities" : qUnion([Q0]), "operationType" : NewBodyOperationType.REMOVE, "oppositeDirection" : true, "depth" : .5 * mm});
        }
        {
            var Q0;
            Q0=makeQuery(id+"F4.opExtrude","CAP_EDGE",EDGE,{"disambiguationData":[OSD([sQuery(id+"F2.wireOp",EDGE,"E671.right")])],"isStart":true});
            fillet(context, id + "F8", {"entities" : qUnion([Q0]), "radius" : 5 * mm, "tangentPropagation" : true, "allowEdgeOverflow" : false});
        }
    });